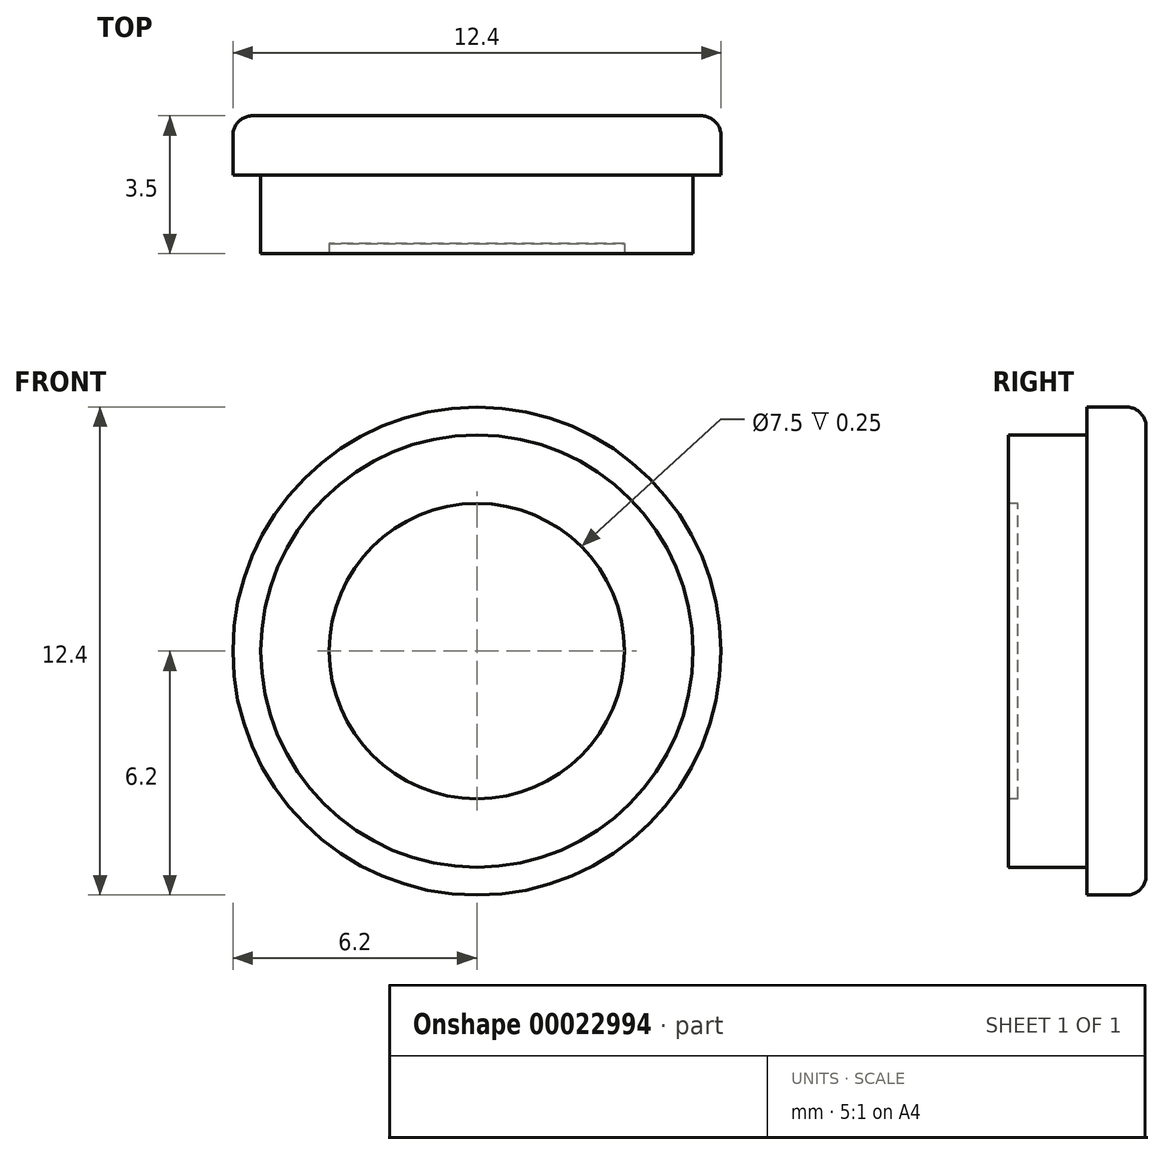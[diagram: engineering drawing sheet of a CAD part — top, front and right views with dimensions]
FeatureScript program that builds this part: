
annotation { "Feature Type Name" : "Feature", "Feature Type Description" : "" }
export const myFeature = defineFeature(function(context is Context, id is Id, definition is map)
    precondition{}
    {
        {
            var Q0;
            Q0=qCreatedBy(makeId("Front.planeOp"),FACE);
            var sketch = newSketch(context, id + "F0", { "sketchPlane" : qUnion([Q0])});
            skCircle(sketch, "E0", {"center": v(0, 0) * mm, "radius": 6.2 * mm});
            skSolve(sketch);
        }
        {
            var Q0;
            Q0 = qSketchRegion(id + "F0", true);
            extrude(context, id + "F1", {"entities" : qUnion([Q0]), "depth" : 1.5 * mm});
        }
        {
            var Q0;
            Q0=makeQuery(id+"F1.opExtrude","CAP_FACE",FACE,{"disambiguationData":[OSD([sQuery(id+"F0.wireOp",EDGE,"E0")])],"isStart":false});
            var sketch = newSketch(context, id + "F2", { "sketchPlane" : qUnion([Q0])});
            skCircle(sketch, "E1", {"center": v(0, 0) * mm, "radius": 5.5 * mm});
            skSolve(sketch);
        }
        {
            var Q0;
            Q0 = qSketchRegion(id + "F2", true);
            extrude(context, id + "F3", {"entities" : qUnion([Q0]), "operationType" : NewBodyOperationType.ADD, "depth" : 2 * mm});
        }
        {
            var Q0;
            Q0=makeQuery(id+"F3.opExtrude","CAP_FACE",FACE,{"disambiguationData":[OSD([sQuery(id+"F2.wireOp",EDGE,"E1")])],"isStart":false});
            var sketch = newSketch(context, id + "F4", { "sketchPlane" : qUnion([Q0])});
            skCircle(sketch, "E2", {"center": v(0, 0) * mm, "radius": 3.75 * mm});
            skSolve(sketch);
        }
        {
            var Q0;
            Q0 = qSketchRegion(id + "F4", true);
            extrude(context, id + "F5", {"entities" : qUnion([Q0]), "operationType" : NewBodyOperationType.REMOVE, "oppositeDirection" : true, "depth" : .25 * mm});
        }
        {
            var Q0;
            Q0=makeQuery(id+"F1.opExtrude","CAP_EDGE",EDGE,{"disambiguationData":[OSD([sQuery(id+"F0.wireOp",EDGE,"E0")])],"isStart":true});
            fillet(context, id + "F6", {"entities" : qUnion([Q0]), "radius" : .5 * mm, "tangentPropagation" : true, "allowEdgeOverflow" : false});
        }
    });
